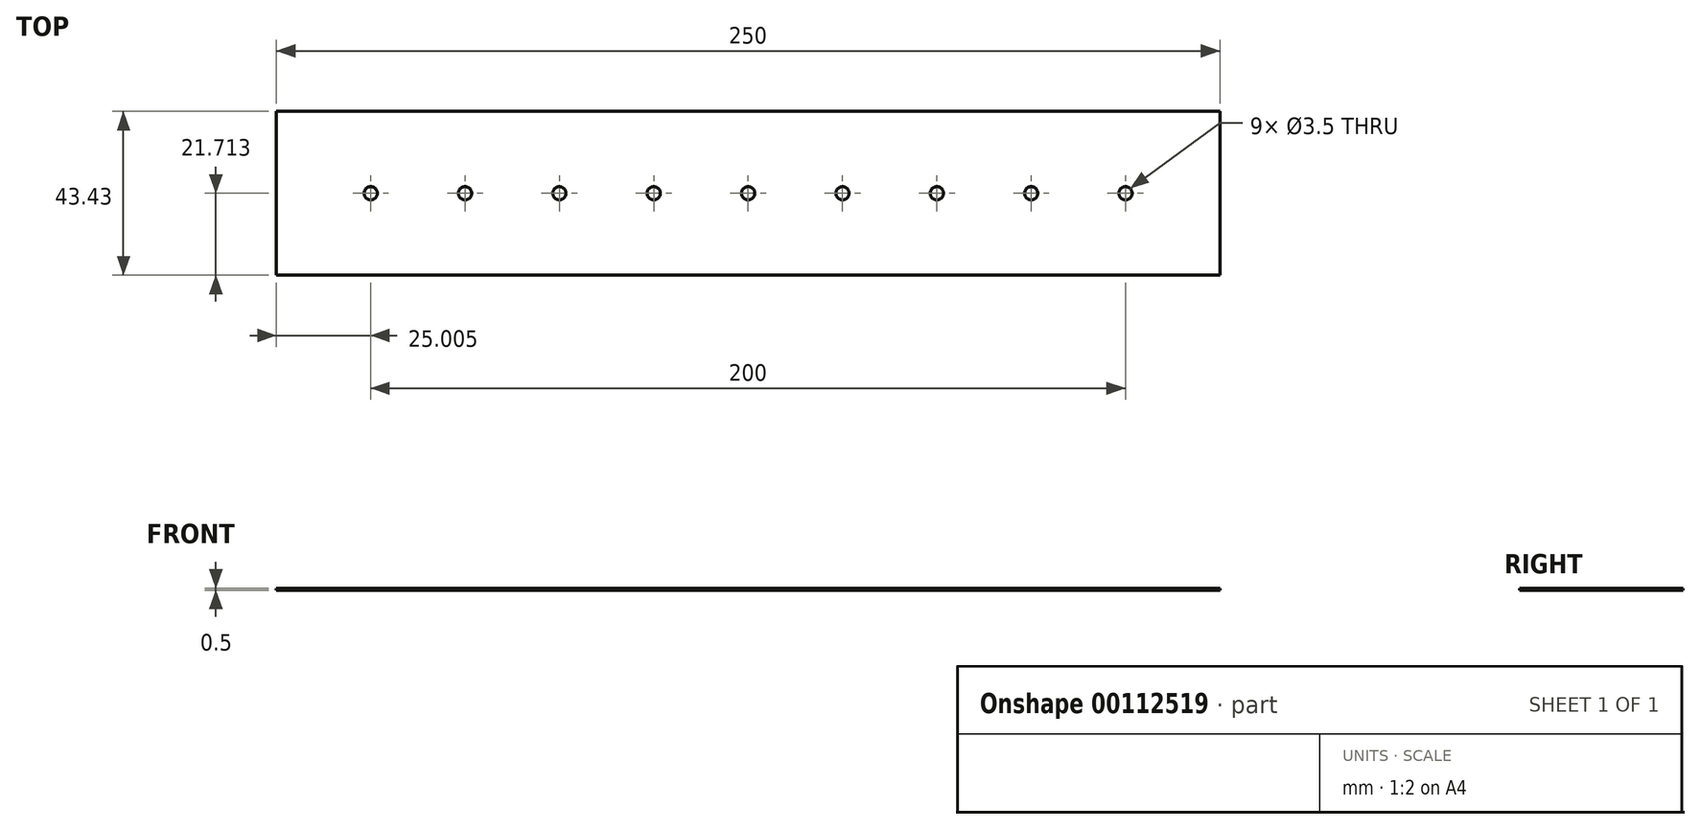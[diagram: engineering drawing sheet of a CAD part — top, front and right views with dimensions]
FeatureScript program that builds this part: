
annotation { "Feature Type Name" : "Feature", "Feature Type Description" : "" }
export const myFeature = defineFeature(function(context is Context, id is Id, definition is map)
    precondition{}
    {
        {
            var Q0;
            Q0=qCreatedBy(makeId("Top.planeOp"),FACE);
            var sketch = newSketch(context, id + "F0", { "sketchPlane" : qUnion([Q0])});
            skLineSegment(sketch, "E0.bottom", {"start": v(-139.89, -43.43) * mm, "end": v(110.11, -43.43) * mm});
            skLineSegment(sketch, "E0.top", {"start": v(-139.89, 0) * mm, "end": v(110.11, 0) * mm});
            skLineSegment(sketch, "E0.left", {"start": v(-139.89, -43.43) * mm, "end": v(-139.89, 0) * mm});
            skLineSegment(sketch, "E0.right", {"start": v(110.11, -43.43) * mm, "end": v(110.11, 0) * mm});
            skCircle(sketch, "E1", {"center": v(-114.89, -21.72) * mm, "radius": 1.75 * mm});
            skLineSegment(sketch, "E2.direction1", {"start": v(-139.89, -21.72) * mm, "end": v(110.11, -21.72) * mm, "construction": true});
            skCircle(sketch, "E3.1.0.0", {"center": v(-89.89, -21.72) * mm, "radius": 1.75 * mm});
            skCircle(sketch, "E3.2.0.0", {"center": v(-64.89, -21.72) * mm, "radius": 1.75 * mm});
            skCircle(sketch, "E3.3.0.0", {"center": v(-39.89, -21.72) * mm, "radius": 1.75 * mm});
            skCircle(sketch, "E3.4.0.0", {"center": v(-14.89, -21.72) * mm, "radius": 1.75 * mm});
            skCircle(sketch, "E3.5.0.0", {"center": v(10.11, -21.72) * mm, "radius": 1.75 * mm});
            skCircle(sketch, "E3.6.0.0", {"center": v(35.11, -21.72) * mm, "radius": 1.75 * mm});
            skCircle(sketch, "E3.7.0.0", {"center": v(60.11, -21.72) * mm, "radius": 1.75 * mm});
            skCircle(sketch, "E3.8.0.0", {"center": v(85.11, -21.72) * mm, "radius": 1.75 * mm});
            skLineSegment(sketch, "E3.direction1", {"start": v(-114.89, -21.72) * mm, "end": v(-89.89, -21.72) * mm, "construction": true});
            skSolve(sketch);
        }
        {
            var Q0;
            Q0=sQuery(id+"F0.wireOp",EDGE,"E1");
            var Q1;
            Q1=sQuery(id+"F0.wireOp",EDGE,"E3.1.0.0");
            var Q2;
            Q2=sQuery(id+"F0.wireOp",EDGE,"E3.2.0.0");
            var Q3;
            Q3=sQuery(id+"F0.wireOp",EDGE,"E3.3.0.0");
            var Q4;
            Q4=sQuery(id+"F0.wireOp",EDGE,"E3.4.0.0");
            var Q5;
            Q5=sQuery(id+"F0.wireOp",EDGE,"E3.5.0.0");
            var Q6;
            Q6=sQuery(id+"F0.wireOp",EDGE,"E3.6.0.0");
            var Q7;
            Q7=sQuery(id+"F0.wireOp",EDGE,"E3.7.0.0");
            var Q8;
            Q8=sQuery(id+"F0.wireOp",EDGE,"E3.8.0.0");
            var Q9;
            Q9=sQuery(id+"F0.wireOp",EDGE,"E3.9.0.0");
            extrude(context, id + "F1", {"bodyType" : ToolBodyType.SURFACE, "surfaceEntities" : qUnion([Q0, Q1, Q2, Q3, Q4, Q5, Q6, Q7, Q8, Q9]), "depth" : 50 * mm});
        }
        {
            var Q0;
            Q0=makeQuery(id+"F0.imprint","IMPRINT",FACE,{"disambiguationData":[TD([[makeQuery(id+"F0.imprint","IMPRINT",EDGE,{"derivedFrom":sQuery(id+"F0.wireOp",EDGE,"E0.bottom")}),1.0]])]});
            extrude(context, id + "F2", {"entities" : qUnion([Q0]), "depth" : 0.5 * mm});
        }
    });
